# Revit family: 3454_NX_Bluetooth_Bridge_Module
name_source: partatom
category: Communication Devices
revit_build: Autodesk Revit 2014 (Build: 20130308_1515(x64)
units: mm (PartAtom-declared; Revit-internal decimal feet)

## types (1)
- 3454_NX_Bluetooth_Bridge_Module
    Assembly Code = D5090
    Default Elevation = 48 "
    Description = The NXBTR Bluetooth® Radio Module provides a wireless communication bridge between the NX Room Controller and an IOS® or Android™ smart phone app
    Features = • Bluetooth Technology (Ver. 4.1)
• Easily pairs with smart phone with active Bluetooth radio
• NX App available for free download from Apple® and Google Play store
• LED status indicates successful connection
• Simple RJ45 plug in connection to NX SmartPORT
• Powered from the SmartPORT
• Low voltage device: 24 VDC
• NXBTC provides real time clock function for scheduling
• NXBTC is cULus listed for use in a return air plenum
    Housing Material = Paint - Hubbell - Carbon Black
    Manufacturer = Hubbell Control Solutions
    Model = NX Bluetooth® Radio Module
    Plug = Glass - Hubbell - White
    Product Documentation Link = https://hubbellcdn.com
    Product Page URL = https://www.hubbell.com
    Type Comments = NX Bluetooth® Radio Module
    URL = https://www.hubbell.com
    Voltage = 24V
    Warranty = 5-Years Warranty

## geometry (parser evidence)
native form markers: Sweep x1
no freeform markers — native parametric forms only
